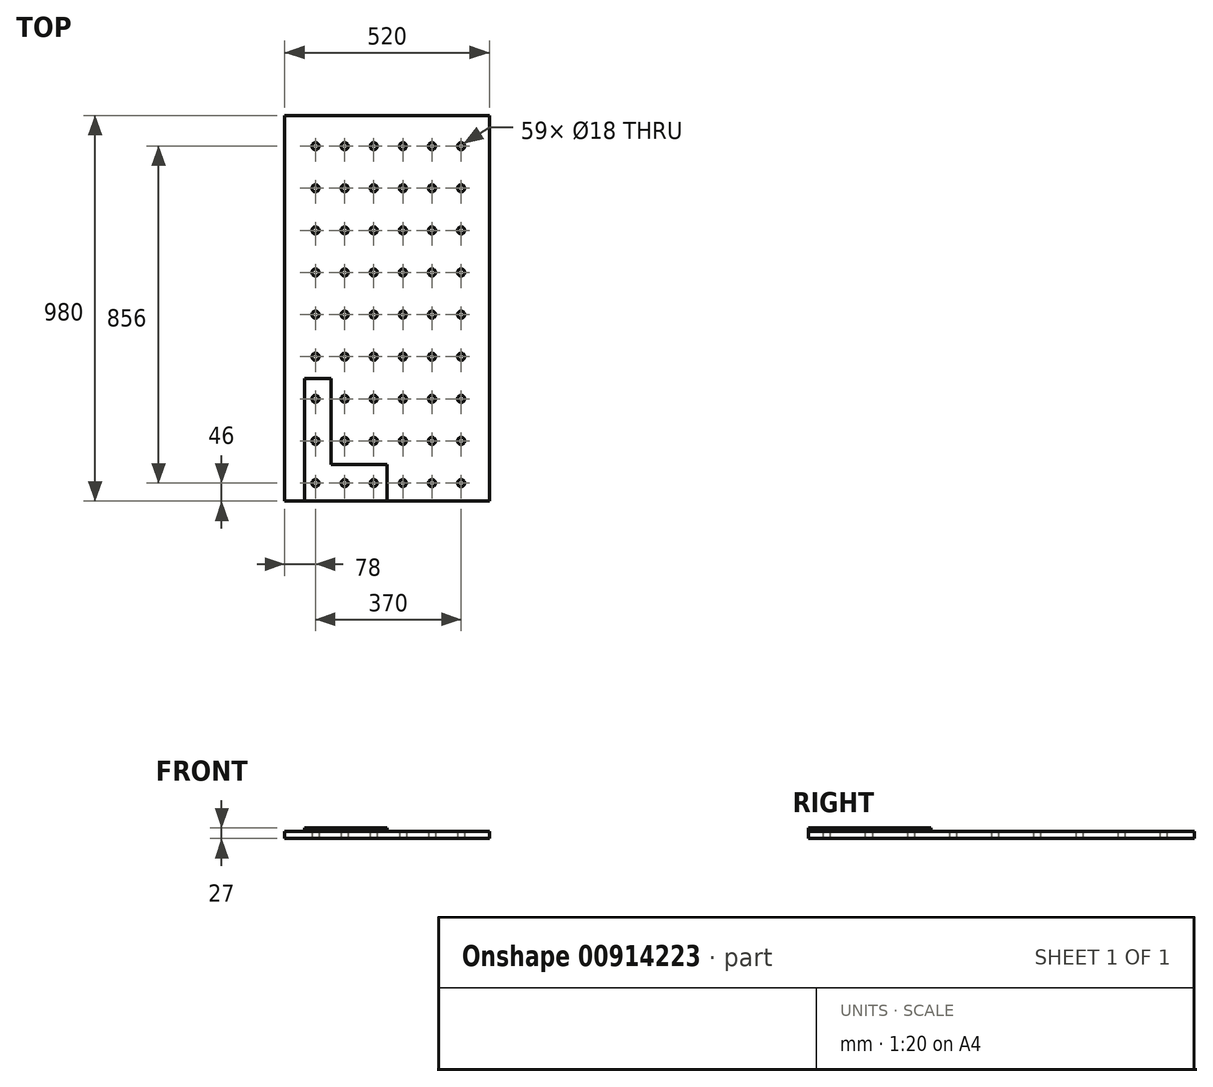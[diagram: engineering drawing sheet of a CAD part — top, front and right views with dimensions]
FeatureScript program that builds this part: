
annotation { "Feature Type Name" : "Feature", "Feature Type Description" : "" }
export const myFeature = defineFeature(function(context is Context, id is Id, definition is map)
    precondition{}
    {
        {
            var Q0;
            Q0=qCreatedBy(makeId("Top.planeOp"),FACE);
            var sketch = newSketch(context, id + "F0", { "sketchPlane" : qUnion([Q0])});
            skLineSegment(sketch, "E0.bottom", {"start": v(-260, 490) * mm, "end": v(260, 490) * mm});
            skLineSegment(sketch, "E0.top", {"start": v(-260, -490) * mm, "end": v(260, -490) * mm});
            skLineSegment(sketch, "E0.left", {"start": v(-260, 490) * mm, "end": v(-260, -490) * mm});
            skLineSegment(sketch, "E0.right", {"start": v(260, 490) * mm, "end": v(260, -490) * mm});
            skPoint(sketch, "E0.middle", {"position": v(0, 0) * mm});
            skCircle(sketch, "E1", {"center": v(-182, 412) * mm, "radius": 9 * mm});
            skCircle(sketch, "E2.0.1.0", {"center": v(-182, 305) * mm, "radius": 9 * mm});
            skCircle(sketch, "E2.0.2.0", {"center": v(-182, 198) * mm, "radius": 9 * mm});
            skCircle(sketch, "E2.0.3.0", {"center": v(-182, 91) * mm, "radius": 9 * mm});
            skCircle(sketch, "E2.0.4.0", {"center": v(-182, -16) * mm, "radius": 9 * mm});
            skCircle(sketch, "E2.0.5.0", {"center": v(-182, -123) * mm, "radius": 9 * mm});
            skCircle(sketch, "E2.0.6.0", {"center": v(-182, -230) * mm, "radius": 9 * mm});
            skCircle(sketch, "E2.0.7.0", {"center": v(-182, -337) * mm, "radius": 9 * mm});
            skCircle(sketch, "E2.0.8.0", {"center": v(-182, -444) * mm, "radius": 9 * mm});
            skCircle(sketch, "E2.1.0.0", {"center": v(-108, 412) * mm, "radius": 9 * mm});
            skCircle(sketch, "E2.1.1.0", {"center": v(-108, 305) * mm, "radius": 9 * mm});
            skCircle(sketch, "E2.1.2.0", {"center": v(-108, 198) * mm, "radius": 9 * mm});
            skCircle(sketch, "E2.1.3.0", {"center": v(-108, 91) * mm, "radius": 9 * mm});
            skCircle(sketch, "E2.1.4.0", {"center": v(-108, -16) * mm, "radius": 9 * mm});
            skCircle(sketch, "E2.1.5.0", {"center": v(-108, -123) * mm, "radius": 9 * mm});
            skCircle(sketch, "E2.1.6.0", {"center": v(-108, -230) * mm, "radius": 9 * mm});
            skCircle(sketch, "E2.1.7.0", {"center": v(-108, -337) * mm, "radius": 9 * mm});
            skCircle(sketch, "E2.1.8.0", {"center": v(-108, -444) * mm, "radius": 9 * mm});
            skCircle(sketch, "E2.2.0.0", {"center": v(-34, 412) * mm, "radius": 9 * mm});
            skCircle(sketch, "E2.2.1.0", {"center": v(-34, 305) * mm, "radius": 9 * mm});
            skCircle(sketch, "E2.2.2.0", {"center": v(-34, 198) * mm, "radius": 9 * mm});
            skCircle(sketch, "E2.2.3.0", {"center": v(-34, 91) * mm, "radius": 9 * mm});
            skCircle(sketch, "E2.2.4.0", {"center": v(-34, -16) * mm, "radius": 9 * mm});
            skCircle(sketch, "E2.2.5.0", {"center": v(-34, -123) * mm, "radius": 9 * mm});
            skCircle(sketch, "E2.2.6.0", {"center": v(-34, -230) * mm, "radius": 9 * mm});
            skCircle(sketch, "E2.2.7.0", {"center": v(-34, -337) * mm, "radius": 9 * mm});
            skCircle(sketch, "E2.2.8.0", {"center": v(-34, -444) * mm, "radius": 9 * mm});
            skCircle(sketch, "E2.3.0.0", {"center": v(40, 412) * mm, "radius": 9 * mm});
            skCircle(sketch, "E2.3.1.0", {"center": v(40, 305) * mm, "radius": 9 * mm});
            skCircle(sketch, "E2.3.2.0", {"center": v(40, 198) * mm, "radius": 9 * mm});
            skCircle(sketch, "E2.3.3.0", {"center": v(40, 91) * mm, "radius": 9 * mm});
            skCircle(sketch, "E2.3.4.0", {"center": v(40, -16) * mm, "radius": 9 * mm});
            skCircle(sketch, "E2.3.5.0", {"center": v(40, -123) * mm, "radius": 9 * mm});
            skCircle(sketch, "E2.3.6.0", {"center": v(40, -230) * mm, "radius": 9 * mm});
            skCircle(sketch, "E2.3.7.0", {"center": v(40, -337) * mm, "radius": 9 * mm});
            skCircle(sketch, "E2.3.8.0", {"center": v(40, -444) * mm, "radius": 9 * mm});
            skCircle(sketch, "E2.4.0.0", {"center": v(114, 412) * mm, "radius": 9 * mm});
            skCircle(sketch, "E2.4.1.0", {"center": v(114, 305) * mm, "radius": 9 * mm});
            skCircle(sketch, "E2.4.2.0", {"center": v(114, 198) * mm, "radius": 9 * mm});
            skCircle(sketch, "E2.4.3.0", {"center": v(114, 91) * mm, "radius": 9 * mm});
            skCircle(sketch, "E2.4.4.0", {"center": v(114, -16) * mm, "radius": 9 * mm});
            skCircle(sketch, "E2.4.5.0", {"center": v(114, -123) * mm, "radius": 9 * mm});
            skCircle(sketch, "E2.4.6.0", {"center": v(114, -230) * mm, "radius": 9 * mm});
            skCircle(sketch, "E2.4.7.0", {"center": v(114, -337) * mm, "radius": 9 * mm});
            skCircle(sketch, "E2.4.8.0", {"center": v(114, -444) * mm, "radius": 9 * mm});
            skCircle(sketch, "E2.5.0.0", {"center": v(188, 412) * mm, "radius": 9 * mm});
            skCircle(sketch, "E2.5.1.0", {"center": v(188, 305) * mm, "radius": 9 * mm});
            skCircle(sketch, "E2.5.2.0", {"center": v(188, 198) * mm, "radius": 9 * mm});
            skCircle(sketch, "E2.5.3.0", {"center": v(188, 91) * mm, "radius": 9 * mm});
            skCircle(sketch, "E2.5.4.0", {"center": v(188, -16) * mm, "radius": 9 * mm});
            skCircle(sketch, "E2.5.5.0", {"center": v(188, -123) * mm, "radius": 9 * mm});
            skCircle(sketch, "E2.5.6.0", {"center": v(188, -230) * mm, "radius": 9 * mm});
            skCircle(sketch, "E2.5.7.0", {"center": v(188, -337) * mm, "radius": 9 * mm});
            skCircle(sketch, "E2.5.8.0", {"center": v(188, -444) * mm, "radius": 9 * mm});
            skLineSegment(sketch, "E2.direction1", {"start": v(-182, 412) * mm, "end": v(-108, 412) * mm, "construction": true});
            skLineSegment(sketch, "E2.direction2", {"start": v(-182, 412) * mm, "end": v(-182, 305) * mm, "construction": true});
            skSolve(sketch);
        }
        {
            var Q0;
            Q0=makeQuery(id+"F0.imprint","IMPRINT",FACE,{"disambiguationData":[TD([[makeQuery(id+"F0.imprint","IMPRINT",EDGE,{"derivedFrom":sQuery(id+"F0.wireOp",EDGE,"E0.bottom")}),-1.0]])]});
            extrude(context, id + "F1", {"entities" : qUnion([Q0]), "depth" : 18 * mm, "offsetDistance" : 25 * mm});
        }
        {
            var Q0;
            Q0=makeQuery(id+"F1.opExtrude","CAP_FACE",FACE,{"disambiguationData":[OSD([sQuery(id+"F0.wireOp",EDGE,"E0.bottom"),sQuery(id+"F0.wireOp",EDGE,"E0.top"),sQuery(id+"F0.wireOp",EDGE,"E0.left"),sQuery(id+"F0.wireOp",EDGE,"E0.right"),sQuery(id+"F0.wireOp",EDGE,"E1"),sQuery(id+"F0.wireOp",EDGE,"E2.0.1.0"),sQuery(id+"F0.wireOp",EDGE,"E2.0.2.0"),sQuery(id+"F0.wireOp",EDGE,"E2.0.3.0"),sQuery(id+"F0.wireOp",EDGE,"E2.0.4.0"),sQuery(id+"F0.wireOp",EDGE,"E2.0.5.0"),sQuery(id+"F0.wireOp",EDGE,"E2.0.6.0"),sQuery(id+"F0.wireOp",EDGE,"E2.0.7.0"),sQuery(id+"F0.wireOp",EDGE,"E2.0.8.0"),sQuery(id+"F0.wireOp",EDGE,"E2.1.0.0"),sQuery(id+"F0.wireOp",EDGE,"E2.1.1.0"),sQuery(id+"F0.wireOp",EDGE,"E2.1.2.0"),sQuery(id+"F0.wireOp",EDGE,"E2.1.3.0"),sQuery(id+"F0.wireOp",EDGE,"E2.1.4.0"),sQuery(id+"F0.wireOp",EDGE,"E2.1.5.0"),sQuery(id+"F0.wireOp",EDGE,"E2.1.6.0"),sQuery(id+"F0.wireOp",EDGE,"E2.1.7.0"),sQuery(id+"F0.wireOp",EDGE,"E2.1.8.0"),sQuery(id+"F0.wireOp",EDGE,"E2.2.0.0"),sQuery(id+"F0.wireOp",EDGE,"E2.2.1.0"),sQuery(id+"F0.wireOp",EDGE,"E2.2.2.0"),sQuery(id+"F0.wireOp",EDGE,"E2.2.3.0"),sQuery(id+"F0.wireOp",EDGE,"E2.2.4.0"),sQuery(id+"F0.wireOp",EDGE,"E2.2.5.0"),sQuery(id+"F0.wireOp",EDGE,"E2.2.6.0"),sQuery(id+"F0.wireOp",EDGE,"E2.2.7.0"),sQuery(id+"F0.wireOp",EDGE,"E2.2.8.0"),sQuery(id+"F0.wireOp",EDGE,"E2.3.0.0"),sQuery(id+"F0.wireOp",EDGE,"E2.3.1.0"),sQuery(id+"F0.wireOp",EDGE,"E2.3.2.0"),sQuery(id+"F0.wireOp",EDGE,"E2.3.3.0"),sQuery(id+"F0.wireOp",EDGE,"E2.3.4.0"),sQuery(id+"F0.wireOp",EDGE,"E2.3.5.0"),sQuery(id+"F0.wireOp",EDGE,"E2.3.6.0"),sQuery(id+"F0.wireOp",EDGE,"E2.3.7.0"),sQuery(id+"F0.wireOp",EDGE,"E2.3.8.0"),sQuery(id+"F0.wireOp",EDGE,"E2.4.0.0"),sQuery(id+"F0.wireOp",EDGE,"E2.4.1.0"),sQuery(id+"F0.wireOp",EDGE,"E2.4.2.0"),sQuery(id+"F0.wireOp",EDGE,"E2.4.3.0"),sQuery(id+"F0.wireOp",EDGE,"E2.4.4.0"),sQuery(id+"F0.wireOp",EDGE,"E2.4.5.0"),sQuery(id+"F0.wireOp",EDGE,"E2.4.6.0"),sQuery(id+"F0.wireOp",EDGE,"E2.4.7.0"),sQuery(id+"F0.wireOp",EDGE,"E2.4.8.0"),sQuery(id+"F0.wireOp",EDGE,"E2.5.0.0"),sQuery(id+"F0.wireOp",EDGE,"E2.5.1.0"),sQuery(id+"F0.wireOp",EDGE,"E2.5.2.0"),sQuery(id+"F0.wireOp",EDGE,"E2.5.3.0"),sQuery(id+"F0.wireOp",EDGE,"E2.5.4.0"),sQuery(id+"F0.wireOp",EDGE,"E2.5.5.0"),sQuery(id+"F0.wireOp",EDGE,"E2.5.6.0"),sQuery(id+"F0.wireOp",EDGE,"E2.5.7.0"),sQuery(id+"F0.wireOp",EDGE,"E2.5.8.0")])],"isStart":false});
            var sketch = newSketch(context, id + "F2", { "sketchPlane" : qUnion([Q0])});
            skLineSegment(sketch, "E3.bottom", {"start": v(0, -490) * mm, "end": v(-260, -490) * mm});
            skLineSegment(sketch, "E3.top", {"start": v(0, -396.27) * mm, "end": v(-142.78, -396.27) * mm});
            skLineSegment(sketch, "E3.left", {"start": v(0, -490) * mm, "end": v(0, -396.27) * mm});
            skLineSegment(sketch, "E3.right", {"start": v(-260, -490) * mm, "end": v(-260, -396.27) * mm});
            skLineSegment(sketch, "E4.bottom", {"start": v(-209.22, -490) * mm, "end": v(-142.78, -490) * mm});
            skLineSegment(sketch, "E4.top", {"start": v(-209.22, -178.42) * mm, "end": v(-142.78, -178.42) * mm});
            skLineSegment(sketch, "E4.right", {"start": v(-142.78, -396.27) * mm, "end": v(-142.78, -178.42) * mm});
            skLineSegment(sketch, "E5", {"start": v(-209.22, -178.42) * mm, "end": v(-209.22, -490) * mm});
            skSolve(sketch);
        }
        {
            var Q0;
            Q0=makeQuery(id+"F2.imprint","IMPRINT",FACE,{"disambiguationData":[TD([[makeQuery(id+"F2.imprint","IMPRINT",EDGE,{"derivedFrom":sQuery(id+"F2.wireOp",EDGE,"E3.top")}),1.0]])]});
            extrude(context, id + "F3", {"entities" : qUnion([Q0]), "depth" : 9 * mm, "offsetDistance" : 25 * mm});
        }
    });
